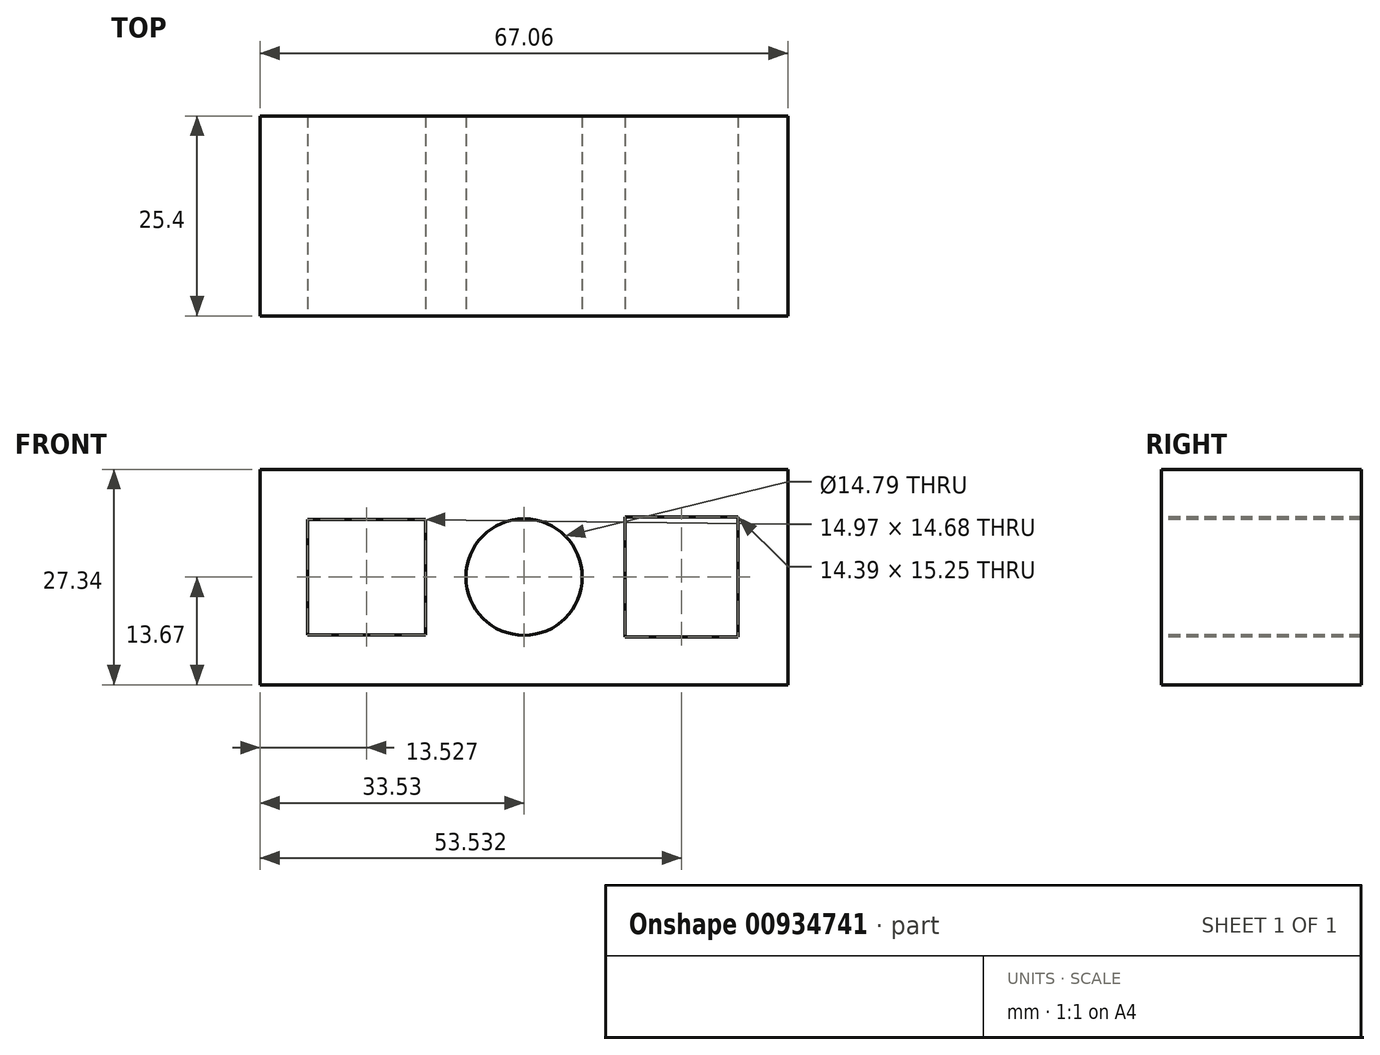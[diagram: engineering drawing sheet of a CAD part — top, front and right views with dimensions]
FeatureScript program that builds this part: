
annotation { "Feature Type Name" : "Feature", "Feature Type Description" : "" }
export const myFeature = defineFeature(function(context is Context, id is Id, definition is map)
    precondition{}
    {
        {
            var Q0;
            Q0=qCreatedBy(makeId("Front.planeOp"),FACE);
            var sketch = newSketch(context, id + "F0", { "sketchPlane" : qUnion([Q0])});
            skLineSegment(sketch, "E0.bottom", {"start": v(-33.53, 13.67) * mm, "end": v(33.53, 13.67) * mm});
            skLineSegment(sketch, "E0.top", {"start": v(-33.53, -13.67) * mm, "end": v(33.53, -13.67) * mm});
            skLineSegment(sketch, "E0.left", {"start": v(-33.53, 13.67) * mm, "end": v(-33.53, -13.67) * mm});
            skLineSegment(sketch, "E0.right", {"start": v(33.53, 13.67) * mm, "end": v(33.53, -13.67) * mm});
            skPoint(sketch, "E0.middle", {"position": v(0, 0) * mm});
            skSolve(sketch);
        }
        {
            var Q0;
            Q0 = qSketchRegion(id + "F0", true);
            extrude(context, id + "F1", {"entities" : qUnion([Q0]), "depth" : 25.4 * mm, "offsetDistance" : 25.4 * mm});
        }
        {
            var Q0;
            Q0=makeQuery(id+"F1.opExtrude","CAP_FACE",FACE,{"disambiguationData":[OSD([sQuery(id+"F0.wireOp",EDGE,"E0.bottom"),sQuery(id+"F0.wireOp",EDGE,"E0.top"),sQuery(id+"F0.wireOp",EDGE,"E0.left"),sQuery(id+"F0.wireOp",EDGE,"E0.right")])],"isStart":false});
            var sketch = newSketch(context, id + "F2", { "sketchPlane" : qUnion([Q0])});
            skLineSegment(sketch, "E1.bottom", {"start": v(-27.49, 7.34) * mm, "end": v(-12.52, 7.34) * mm});
            skLineSegment(sketch, "E1.top", {"start": v(-27.49, -7.34) * mm, "end": v(-12.52, -7.34) * mm});
            skLineSegment(sketch, "E1.left", {"start": v(-27.49, 7.34) * mm, "end": v(-27.49, -7.34) * mm});
            skLineSegment(sketch, "E1.right", {"start": v(-12.52, 7.34) * mm, "end": v(-12.52, -7.34) * mm});
            skPoint(sketch, "E1.middle", {"position": v(-20, 0) * mm});
            skSolve(sketch);
        }
        {
            var Q0;
            Q0 = qSketchRegion(id + "F2", true);
            extrude(context, id + "F3", {"entities" : qUnion([Q0]), "operationType" : NewBodyOperationType.REMOVE, "oppositeDirection" : true, "depth" : 25.4 * mm, "offsetDistance" : 25.4 * mm});
        }
        {
            var Q0;
            Q0=makeQuery(id+"F1.opExtrude","CAP_FACE",FACE,{"disambiguationData":[OSD([sQuery(id+"F0.wireOp",EDGE,"E0.bottom"),sQuery(id+"F0.wireOp",EDGE,"E0.top"),sQuery(id+"F0.wireOp",EDGE,"E0.left"),sQuery(id+"F0.wireOp",EDGE,"E0.right")])],"isStart":false});
            var sketch = newSketch(context, id + "F4", { "sketchPlane" : qUnion([Q0])});
            skCircle(sketch, "E2", {"center": v(0, 0) * mm, "radius": 7.4 * mm});
            skSolve(sketch);
        }
        {
            var Q0;
            Q0 = qSketchRegion(id + "F4", true);
            extrude(context, id + "F5", {"entities" : qUnion([Q0]), "operationType" : NewBodyOperationType.REMOVE, "oppositeDirection" : true, "depth" : 25.4 * mm, "offsetDistance" : 25.4 * mm});
        }
        {
            var Q0;
            Q0=makeQuery(id+"F1.opExtrude","CAP_FACE",FACE,{"disambiguationData":[OSD([sQuery(id+"F0.wireOp",EDGE,"E0.bottom"),sQuery(id+"F0.wireOp",EDGE,"E0.top"),sQuery(id+"F0.wireOp",EDGE,"E0.left"),sQuery(id+"F0.wireOp",EDGE,"E0.right")])],"isStart":false});
            var sketch = newSketch(context, id + "F6", { "sketchPlane" : qUnion([Q0])});
            skLineSegment(sketch, "E3.bottom", {"start": v(12.8, 7.63) * mm, "end": v(27.2, 7.63) * mm});
            skLineSegment(sketch, "E3.top", {"start": v(12.8, -7.63) * mm, "end": v(27.2, -7.63) * mm});
            skLineSegment(sketch, "E3.left", {"start": v(12.8, 7.63) * mm, "end": v(12.8, -7.63) * mm});
            skLineSegment(sketch, "E3.right", {"start": v(27.2, 7.63) * mm, "end": v(27.2, -7.63) * mm});
            skPoint(sketch, "E3.middle", {"position": v(20, 0) * mm});
            skSolve(sketch);
        }
        {
            var Q0;
            Q0 = qSketchRegion(id + "F6", true);
            extrude(context, id + "F7", {"entities" : qUnion([Q0]), "operationType" : NewBodyOperationType.REMOVE, "oppositeDirection" : true, "depth" : 25.4 * mm, "offsetDistance" : 25.4 * mm});
        }
    });
